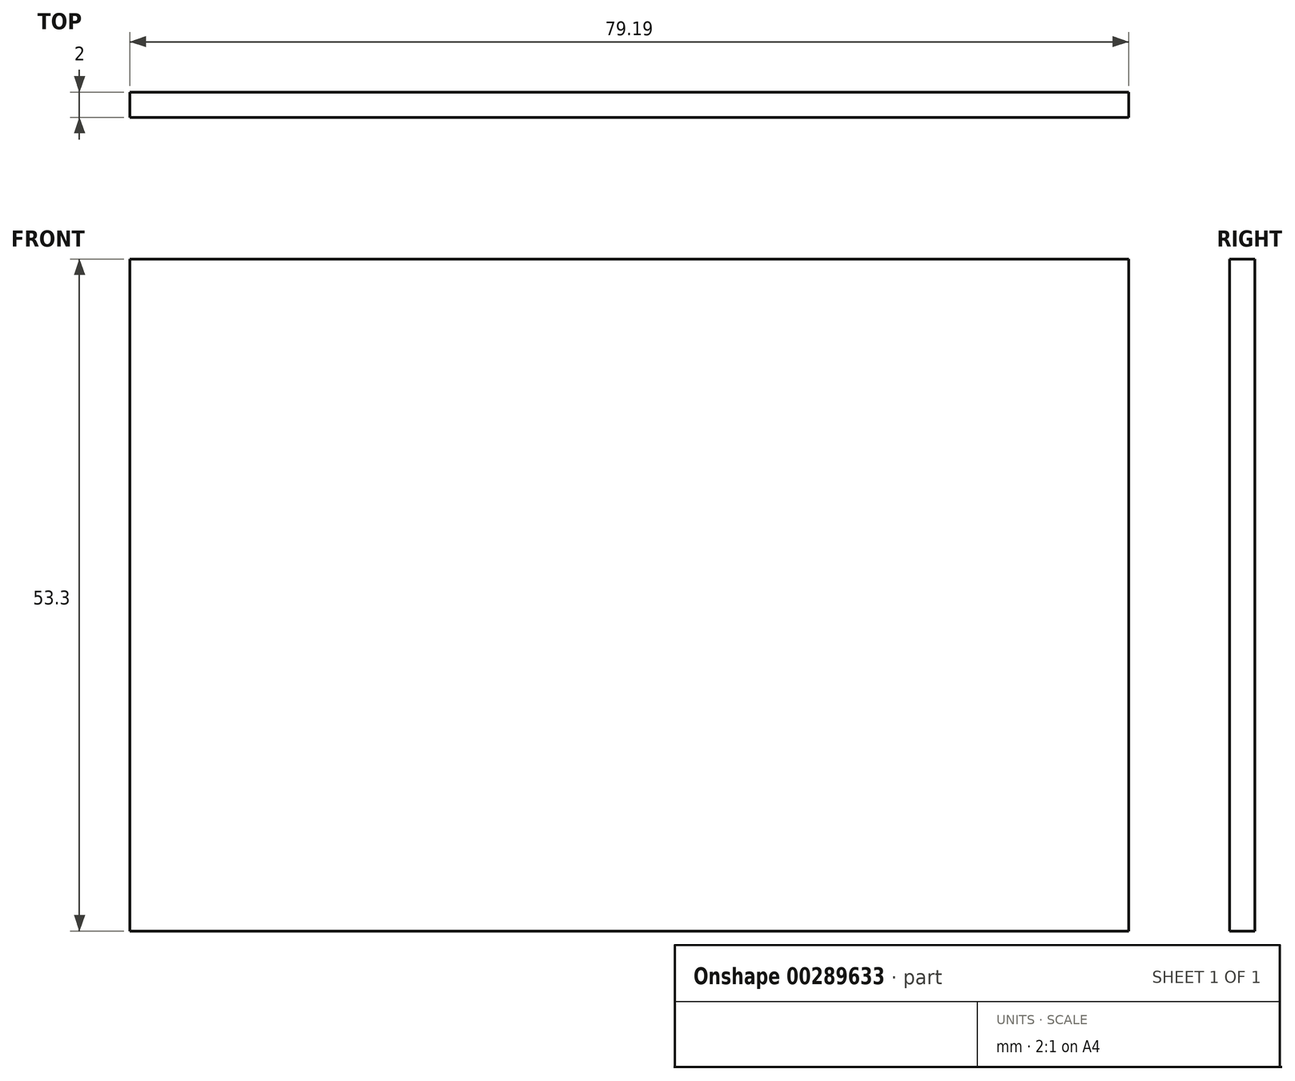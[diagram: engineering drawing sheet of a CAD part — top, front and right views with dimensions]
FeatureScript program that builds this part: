
annotation { "Feature Type Name" : "Feature", "Feature Type Description" : "" }
export const myFeature = defineFeature(function(context is Context, id is Id, definition is map)
    precondition{}
    {
        {
            var Q0;
            Q0=qCreatedBy(makeId("Front.planeOp"),FACE);
            var sketch = newSketch(context, id + "F0", { "sketchPlane" : qUnion([Q0])});
            skLineSegment(sketch, "E0.bottom", {"start": v(-54.48, 33.2) * mm, "end": v(24.71, 33.2) * mm});
            skLineSegment(sketch, "E0.top", {"start": v(-54.48, -20.1) * mm, "end": v(24.71, -20.1) * mm});
            skLineSegment(sketch, "E0.left", {"start": v(-54.48, 33.2) * mm, "end": v(-54.48, -20.1) * mm});
            skLineSegment(sketch, "E0.right", {"start": v(24.71, 33.2) * mm, "end": v(24.71, -20.1) * mm});
            skSolve(sketch);
        }
        {
            var Q0;
            Q0=makeQuery(id+"F0.imprint","IMPRINT",FACE,{"disambiguationData":[TD([[makeQuery(id+"F0.imprint","IMPRINT",EDGE,{"derivedFrom":sQuery(id+"F0.wireOp",EDGE,"E0.bottom")}),-1.0]])]});
            extrude(context, id + "F1", {"entities" : qUnion([Q0]), "depth" : 2 * mm});
        }
    });
